# Revit family: LAMP_KOMBIC 100 SURFACE 2500 CRI80 OPTIC DALI
name_source: partatom
category: Luminarias
revit_build: Autodesk Revit 2018 (Build: 20190510_1515(x64)
units: mm (PartAtom-declared; Revit-internal decimal feet)

## family parameters
Anfitrión = Cara
Compartido = No
Corte con vacíos al cargar = No
Cota de conector redondo = Diámetro de uso
Origen de luz = Sí
Punto de cálculo de habitación = No
Tipo de pieza = Normal

## types (12) — shared parameters
CRI = 80
Cambio de temperatura de color de luz atenuada = <Ninguno>
Diameter = 100 mm  [stored 0.328084 ft]
Elevación por defecto = 1219 mm
Fabricante = LAMP
Filtro de color = 16777215
Gear = Electronic
Height = 180 mm  [stored 0.590551 ft]
IEE = A+
Installation instructions = https://www.lamp.es
Insulation class = I
LED Lifetime = 50.000 L70 B10
Lamp = COB LED
Last update = 29/07/2021
Luminaire type = Suspended
MacAdam = 3
Manufacturer URL = http://www.lamp.es
Manufacturer country = Spain
Manufacturer name = LAMP
Material LED = LAMP_COB
Material cable suspension = LAMP_Acero genérico
Material optica = LAMP_PMMA Optica Kombic100
Model explanation = Possibility of chossing between surface or suspended within the model
Plum = 22 W
Power = 18 W
Power Supply = 220-240V 50/60Hz
Product URL = https://www.lamp.es
Product datasheet = http://www.lamp.es
Protection rating = IP40
Type = COB PHILIPS
Weight = 0.68 kg
Ángulo de inclinación = -90.00°

## per-type parameters (varying)
| type | Archivo de red fotométrica | Efficacy | Finish | Material cuerpo | Material floron | Material reflector | Modelo | Product code | UGR |
| 1609LM 3000K  B/B | K11SF2540WF830NBB.IES | 75 lm/W | Matte black RAL 9011 | LAMP_Plástico genérico NG | LAMP_Plástico genérico NG | LAMP_PC Reflector Kombic Metalizado Negro | K11SF2540WF830DBB | K11SF2540WF830DBB | 17 |
| 1609LM 3000K  B/W | K11SF2540WF830NBW.IES | 75 lm/W | Matte Traffic white RAL 9016 | LAMP_Plástico genérico BL | LAMP_Plástico genérico BL | LAMP_PC Reflector Kombic Metalizado Negro | K11SF2540WF830DBW | K11SF2540WF830DBW | 17 |
| 1692LM 3000K  M/B | K11SF2540WF830NMB.IES | 78 lm/W | Matte black RAL 9011 | LAMP_Plástico genérico NG | LAMP_Plástico genérico NG | LAMP_PC Reflector Kombic Metalizado Mate | K11SF2540WF830DMB | K11SF2540WF830DMB | 17 |
| 1692LM 3000K  M/W | K11SF2540WF830NMW.IES | 78 lm/W | Matte Traffic white RAL 9016 | LAMP_Plástico genérico BL | LAMP_Plástico genérico BL | LAMP_PC Reflector Kombic Metalizado Mate | K11SF2540WF830DMW | K11SF2540WF830DMW | 17 |
| 1701LM 3000K  W/B | K11SF2540WF830NWB.IES | 79 lm/W | Matte black RAL 9011 | LAMP_Plástico genérico NG | LAMP_Plástico genérico NG | LAMP_PC Reflector Kombic Blanco | K11SF2540WF830DWB | K11SF2540WF830DWB | 19 |
| 1701LM 3000K  W/W | K11SF2540WF830NWW.IES | 79 lm/W | Matte Traffic white RAL 9016 | LAMP_Plástico genérico BL | LAMP_Plástico genérico BL | LAMP_PC Reflector Kombic Blanco | K11SF2540WF830DWW | K11SF2540WF830DWW | 19 |
| 1704LM 4000K  B/B | K11SF2540WF840NBB.IES | 79 lm/W | Matte black RAL 9011 | LAMP_Plástico genérico NG | LAMP_Plástico genérico NG | LAMP_PC Reflector Kombic Metalizado Negro | K11SF2540WF840DBB | K11SF2540WF840DBB | 17 |
| 1704LM 4000K  B/W | K11SF2540WF840NBW.IES | 79 lm/W | Matte Traffic white RAL 9016 | LAMP_Plástico genérico BL | LAMP_Plástico genérico BL | LAMP_PC Reflector Kombic Metalizado Negro | K11SF2540WF840DBW | K11SF2540WF840DBW | 17 |
| 1792LM 4000K  M/B | K11SF2540WF840NMB.IES | 83 lm/W | Matte black RAL 9011 | LAMP_Plástico genérico NG | LAMP_Plástico genérico NG | LAMP_PC Reflector Kombic Metalizado Mate | K11SF2540WF840DMB | K11SF2540WF840DMB | 17 |
| 1792LM 4000K  M/W | K11SF2540WF840NMW.IES | 83 lm/W | Matte Traffic white RAL 9016 | LAMP_Plástico genérico BL | LAMP_Plástico genérico BL | LAMP_PC Reflector Kombic Metalizado Mate | K11SF2540WF840DMW | K11SF2540WF840DMW | 17 |
| 1802LM 4000K  W/B | K11SF2540WF840NWB.IES | 83 lm/W | Matte black RAL 9011 | LAMP_Plástico genérico NG | LAMP_Plástico genérico NG | LAMP_PC Reflector Kombic Blanco | K11SF2540WF840DWB | K11SF2540WF840DWB | 19 |
| 1802LM 4000K  W/W | K11SF2540WF840NWW.IES | 83 lm/W | Matte Traffic white RAL 9016 | LAMP_Plástico genérico BL | LAMP_Plástico genérico BL | LAMP_PC Reflector Kombic Blanco | K11SF2540WF840DWW | K11SF2540WF840DWW | 19 |

note: [stored X ft] marks values corroborated as IEEE doubles in the binary element streams (Revit-internal decimal feet)
